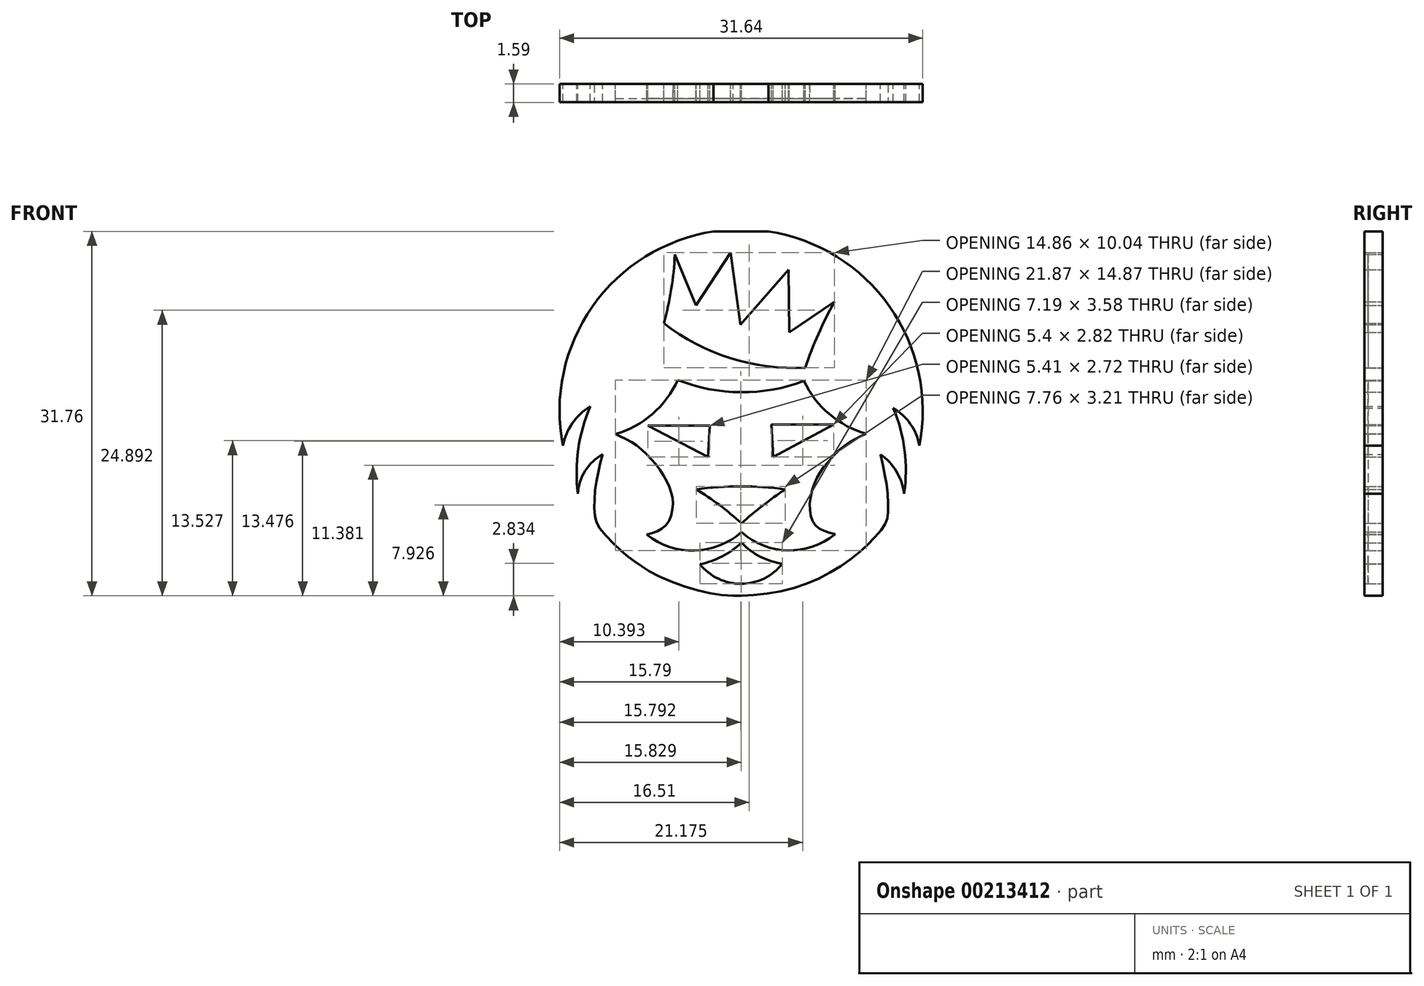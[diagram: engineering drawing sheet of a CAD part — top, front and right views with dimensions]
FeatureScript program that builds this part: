
annotation { "Feature Type Name" : "Feature", "Feature Type Description" : "" }
export const myFeature = defineFeature(function(context is Context, id is Id, definition is map)
    precondition{}
    {
        {
            var Q0;
            Q0=qCreatedBy(makeId("Front.planeOp"),FACE);
            var sketch = newSketch(context, id + "F0", { "sketchPlane" : qUnion([Q0])});
            skLineSegment(sketch, "E0.bottom", {"start": v(15.88, 15.88) * mm, "end": v(-15.87, 15.88) * mm});
            skLineSegment(sketch, "E0.top", {"start": v(15.87, -15.88) * mm, "end": v(-15.88, -15.88) * mm});
            skLineSegment(sketch, "E0.left", {"start": v(15.88, 15.88) * mm, "end": v(15.87, -15.88) * mm});
            skLineSegment(sketch, "E0.right", {"start": v(-15.87, 15.88) * mm, "end": v(-15.88, -15.88) * mm});
            skPoint(sketch, "E0.middle", {"position": v(0, 0) * mm});
            skArc(sketch, "E1", {"start": v(-13.17, 0.62) * mm, "mid": v(-14.22, -3.1) * mm, "end": v(-14.25, -6.97) * mm});
            skArc(sketch, "E2", {"start": v(-12.1, -3.55) * mm, "mid": v(-13.6, -4.99) * mm, "end": v(-14.25, -6.97) * mm});
            skArc(sketch, "E3", {"start": v(-13.17, 0.62) * mm, "mid": v(-14.72, -0.84) * mm, "end": v(-15.56, -2.79) * mm});
            skArc(sketch, "E4", {"start": v(15.5, -2.79) * mm, "mid": v(-0.03, 16.06) * mm, "end": v(-15.56, -2.79) * mm});
            skArc(sketch, "E5", {"start": v(15.5, -2.79) * mm, "mid": v(14.72, -0.9) * mm, "end": v(13.22, 0.47) * mm});
            skArc(sketch, "E6", {"start": v(14.17, -6.97) * mm, "mid": v(14.21, -3.18) * mm, "end": v(13.22, 0.47) * mm});
            skArc(sketch, "E7", {"start": v(14.17, -6.97) * mm, "mid": v(13.5, -5.04) * mm, "end": v(12.1, -3.55) * mm});
            skFitSpline(sketch, "E8", {"points": [v(12.1, -3.55) * mm, v(12.34, -4.64) * mm, v(12.7, -6.62) * mm, v(12.74, -8.8) * mm, v(12.52, -9.63) * mm, v(11.18, -11.24) * mm, v(8.52, -13.38) * mm, v(4.5, -15.2) * mm, v(0, -15.88) * mm, v(-3.35, -15.52) * mm, v(-7.34, -14.1) * mm, v(-9.2, -12.97) * mm, v(-10.56, -11.89) * mm, v(-12.32, -10) * mm, v(-12.74, -9.04) * mm, v(-12.8, -7.46) * mm, v(-12.57, -5.56) * mm, v(-12.1, -3.55) * mm], "startDerivative": vector(5.4, -25.02) * mm, "endDerivative": vector(9.32, 36.32) * mm});
            skArc(sketch, "E9", {"start": v(-6.77, 7.87) * mm, "mid": v(-6.1, 10.84) * mm, "end": v(-5.8, 13.88) * mm});
            skArc(sketch, "E10", {"start": v(-6.77, 7.87) * mm, "mid": v(-0.95, 4.83) * mm, "end": v(5.57, 4) * mm});
            skLineSegment(sketch, "E11", {"start": v(-5.8, 13.88) * mm, "end": v(-3.95, 9.43) * mm});
            skLineSegment(sketch, "E12", {"start": v(-3.95, 9.43) * mm, "end": v(-0.93, 14.03) * mm});
            skLineSegment(sketch, "E13", {"start": v(-0.93, 14.03) * mm, "end": v(-0.08, 7.74) * mm});
            skLineSegment(sketch, "E14", {"start": v(-0.08, 7.74) * mm, "end": v(4.12, 12.55) * mm});
            skLineSegment(sketch, "E15", {"start": v(4.12, 12.55) * mm, "end": v(4.18, 7.08) * mm});
            skLineSegment(sketch, "E16", {"start": v(4.18, 7.08) * mm, "end": v(8.09, 9.73) * mm});
            skArc(sketch, "E17", {"start": v(8.09, 9.73) * mm, "mid": v(6.7, 6.93) * mm, "end": v(5.57, 4) * mm});
            skArc(sketch, "E18", {"start": v(-5.55, 2.94) * mm, "mid": v(-0.06, 1.86) * mm, "end": v(5.45, 2.85) * mm});
            skArc(sketch, "E19", {"start": v(5.45, 2.85) * mm, "mid": v(7.66, -0.04) * mm, "end": v(10.87, -1.74) * mm});
            skArc(sketch, "E20", {"start": v(-11, -1.79) * mm, "mid": v(-7.75, -0.02) * mm, "end": v(-5.55, 2.94) * mm});
            skArc(sketch, "E21", {"start": v(-8.26, -10.54) * mm, "mid": v(-4.1, -11.93) * mm, "end": v(0, -10.33) * mm});
            skArc(sketch, "E22", {"start": v(0, -10.33) * mm, "mid": v(4.05, -11.93) * mm, "end": v(8.16, -10.5) * mm});
            skLineSegment(sketch, "E23", {"start": v(8.03, -0.94) * mm, "end": v(2.62, -0.94) * mm});
            skLineSegment(sketch, "E24", {"start": v(2.62, -0.94) * mm, "end": v(2.78, -3.76) * mm});
            skLineSegment(sketch, "E25", {"start": v(2.78, -3.76) * mm, "end": v(8.03, -0.94) * mm});
            skLineSegment(sketch, "E26", {"start": v(-2.9, -3.76) * mm, "end": v(-2.75, -1.04) * mm});
            skLineSegment(sketch, "E27", {"start": v(-2.75, -1.04) * mm, "end": v(-8.16, -1.04) * mm});
            skLineSegment(sketch, "E28", {"start": v(-8.16, -1.04) * mm, "end": v(-2.9, -3.76) * mm});
            skFitSpline(sketch, "E29", {"points": [v(10.87, -1.74) * mm, v(9, -2.77) * mm, v(7.54, -4.21) * mm, v(6.4, -5.96) * mm, v(5.96, -8.46) * mm, v(6.62, -9.9) * mm, v(8.16, -10.5) * mm], "startDerivative": vector(-11.35, -5.33) * mm, "endDerivative": vector(11.33, -2.74) * mm});
            skFitSpline(sketch, "E30", {"points": [v(-11, -1.79) * mm, v(-9.67, -2.42) * mm, v(-8.31, -3.5) * mm, v(-7.02, -5.02) * mm, v(-6.21, -6.55) * mm, v(-5.97, -7.87) * mm, v(-6.3, -9.33) * mm, v(-7.09, -10.12) * mm, v(-8.26, -10.54) * mm], "startDerivative": vector(10.82, -4.55) * mm, "endDerivative": vector(-10.83, -3.05) * mm});
            skArc(sketch, "E31", {"start": v(3.82, -6.59) * mm, "mid": v(-0.06, -6.35) * mm, "end": v(-3.94, -6.59) * mm});
            skArc(sketch, "E32", {"start": v(3.82, -6.59) * mm, "mid": v(1.86, -8.01) * mm, "end": v(0, -9.56) * mm});
            skArc(sketch, "E33", {"start": v(0, -9.56) * mm, "mid": v(-1.9, -7.98) * mm, "end": v(-3.94, -6.59) * mm});
            skArc(sketch, "E34", {"start": v(0, -11.25) * mm, "mid": v(1.63, -12.47) * mm, "end": v(3.57, -13.09) * mm});
            skArc(sketch, "E35", {"start": v(-3.62, -13.12) * mm, "mid": v(-1.68, -12.44) * mm, "end": v(0, -11.25) * mm});
            skArc(sketch, "E36", {"start": v(-3.62, -13.12) * mm, "mid": v(-0.01, -14.84) * mm, "end": v(3.57, -13.09) * mm});
            skSolve(sketch);
        }
        {
            var Q0;
            Q0=makeQuery(id+"F0.imprint","IMPRINT",FACE,{"disambiguationData":[TD([[makeQuery(id+"F0.imprint","IMPRINT",EDGE,{"derivedFrom":sQuery(id+"F0.wireOp",EDGE,"E1")}),1.0]])]});
            var Q1;
            Q1=makeQuery(id+"F0.imprint","IMPRINT",FACE,{"disambiguationData":[TD([[makeQuery(id+"F0.imprint","IMPRINT",EDGE,{"derivedFrom":sQuery(id+"F0.wireOp",EDGE,"E26")}),1.0]])]});
            var Q2;
            Q2=makeQuery(id+"F0.imprint","IMPRINT",FACE,{"disambiguationData":[TD([[makeQuery(id+"F0.imprint","IMPRINT",EDGE,{"derivedFrom":sQuery(id+"F0.wireOp",EDGE,"E31")}),1.0]])]});
            var Q3;
            Q3=makeQuery(id+"F0.imprint","IMPRINT",FACE,{"disambiguationData":[TD([[makeQuery(id+"F0.imprint","IMPRINT",EDGE,{"derivedFrom":sQuery(id+"F0.wireOp",EDGE,"E23")}),1.0]])]});
            extrude(context, id + "F1", {"entities" : qUnion([Q0, Q1, Q2, Q3]), "depth" : 1.59 * mm});
        }
        {
            var Q0;
            Q0=makeQuery(id+"F0.imprint","IMPRINT",FACE,{"disambiguationData":[TD([[makeQuery(id+"F0.imprint","IMPRINT",EDGE,{"derivedFrom":sQuery(id+"F0.wireOp",EDGE,"E18")}),-1.0]])]});
            var Q1;
            Q1=makeQuery(id+"F0.imprint","IMPRINT",FACE,{"disambiguationData":[TD([[makeQuery(id+"F0.imprint","IMPRINT",EDGE,{"derivedFrom":sQuery(id+"F0.wireOp",EDGE,"E9")}),-1.0]])]});
            var Q2;
            Q2=makeQuery(id+"F0.imprint","IMPRINT",FACE,{"disambiguationData":[TD([[makeQuery(id+"F0.imprint","IMPRINT",EDGE,{"derivedFrom":sQuery(id+"F0.wireOp",EDGE,"E34")}),-1.0]])]});
            extrude(context, id + "F2", {"entities" : qUnion([Q0, Q1, Q2]), "depth" : 1.27 * mm});
        }
    });
